# Revit family: Sigma_Compact_DN032_s vyp_RFA_2018
name_source: partatom
category: Pipe Accessories
revit_build: Autodesk Revit LT 2018 (Build: 20180329_1100(x64)
units: mm (PartAtom-declared; Revit-internal decimal feet)

## family parameters
Always vertical = Yes
Cut with Voids When Loaded = No
Part Type = Valve - Breaks Into
Round Connector Dimension = Use Diameter
Shared = No
Work Plane-Based = No

## types (3) — shared parameters
C0D0 = No
C0D1 = Yes
CAT0 = Yes
CenSd_R2_6 = 26 mm  [stored 0.0853018 ft]
DR0 = No
DR1 = Yes
Description = Automatický vyvažovací ventil
L2D = 82 mm  [stored 0.269029 ft]
L2D_Min = 30 mm  [stored 0.0984252 ft]
L3 = 25 mm  [stored 0.082021 ft]
LLL = 11 mm  [stored 0.0360892 ft]
MC Pressure Drop Maximum Value = 0.0 Pa
MC Pressure Drop Minimum Value = 0.0 Pa
MC Use Limits From Balancing Method = No
Manufacturer = Hydronic Systems Prague s.r.o.
QmdConnectorList = 301;D;302;D
R1 = 32 mm  [stored 0.104987 ft]
R2 = 31 mm  [stored 0.101706 ft]
R3 = 10 mm  [stored 0.0328084 ft]
R4 = 15 mm  [stored 0.0492126 ft]
Type Comments = závitový; vnitřní závit; PN25; max dp=400kPa; -10~+120°C; max uzavírací tlak 1MPa
URL = www.hydronic.cz
W2D = 32 mm  [stored 0.104987 ft]
XR1 = 26 mm  [stored 0.0853018 ft]
XR2 = 38 mm
magiPartTypeId = 304
magiProductFamilyId = 2dc1766e7e3844cdb739145bbea09c
zero-valued in all types: MC Throttling Maximum Value, MC Throttling Minimum Value

## per-type parameters (varying)
| type | D | DL2 | LL | LL2 | LL3 | LLT | LLT__ve | LL__ve | LM | LP | M2 | M3 | M4 | M5 | MC Product Code | NL | NL__ve | Z2 | Z3 | Z4 | Z5 | Z6 | magiProductId |
| Sigma Compact DN 32 s vypouštěním | 32 mm | 77 mm  [stored 0.252625 ft] | 7 mm  [stored 0.0229659 ft] | 43 mm  [stored 0.141076 ft] | 52 mm  [stored 0.170604 ft] | 23 mm | -23 mm  [stored -0.0754593 ft] | -7 mm  [stored -0.0229659 ft] | 62 mm | 52 mm  [stored 0.170604 ft] | 31 mm  [stored 0.101706 ft] | 33 mm  [stored 0.108268 ft] | 39 mm | 41 mm | 53-2225 DN32 FF s měřením a vypouštěním; (200-5000 l/h); kvs=10,9 | 21 mm  [stored 0.0688976 ft] | -21 mm | 55 mm  [stored 0.180446 ft] | 11 mm  [stored 0.0360892 ft] | 66 mm  [stored 0.216535 ft] | 77 mm  [stored 0.252625 ft] | 33 mm  [stored 0.108268 ft] | 52c1318164f948b8bfa512d8a8b026 |
| Sigma Compact DN 40 s vypouštěním | 40 mm | 79 mm  [stored 0.259186 ft] | 7 mm  [stored 0.0229659 ft] | 45 mm  [stored 0.147638 ft] | 54 mm  [stored 0.177165 ft] | 24 mm  [stored 0.0787402 ft] | -24 mm  [stored -0.0787402 ft] | -7 mm  [stored -0.0229659 ft] | 83 mm | 69 mm  [stored 0.226378 ft] | 41 mm | 43 mm  [stored 0.141076 ft] | 49 mm | 51 mm  [stored 0.167323 ft] | 53-2226 DN40 FF s měřením a vypouštěním; (719-7400 l/h); kvs=18,0 | 28 mm | -28 mm | 66 mm  [stored 0.216535 ft] | 13 mm | 79 mm  [stored 0.259186 ft] | 92 mm | 39 mm | ead7fbe154ec4086ae4626bbcbe652 |
| Sigma Compact DN 50 s vypouštěním | 50 mm | 85 mm | 8 mm  [stored 0.0262467 ft] | 51 mm  [stored 0.167323 ft] | 60 mm  [stored 0.19685 ft] | 28 mm | -28 mm | -8 mm  [stored -0.0262467 ft] | 83 mm | 69 mm  [stored 0.226378 ft] | 41 mm | 43 mm  [stored 0.141076 ft] | 49 mm | 51 mm  [stored 0.167323 ft] | 53-2227 DN50 FF s měřením a vypouštěním; (900-10350 l/h); kvs=20,3 | 28 mm | -28 mm | 66 mm  [stored 0.216535 ft] | 13 mm | 79 mm  [stored 0.259186 ft] | 92 mm | 39 mm | 001ad4382b874bb9b8e1e8cf3b6430 |

note: [stored X ft] marks values corroborated as IEEE doubles in the binary element streams (Revit-internal decimal feet)

## geometry (parser evidence)
native form markers: Sweep x1
no freeform markers — native parametric forms only
